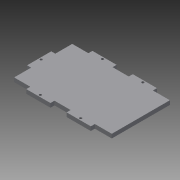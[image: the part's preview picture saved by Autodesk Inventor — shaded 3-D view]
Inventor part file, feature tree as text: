
AUTODESK INVENTOR PART (.ipt)
format: ipt  version: 2014 (Build 180170000, 170)  size: 110,080 bytes
history: native  units: mm
features: reference x4, extrude x1, sketch x1
ambient origin geometry x8: Origin, YZ Plane, XZ Plane, XY Plane, X Axis, Y Axis, Z Axis, Center Point
bodies: 实体1 (feature_tree)
feature tree (6):
  extrude  "拉伸1"  Depth=30.0mm
  sketch  "草图1"  dims[d0=30.0mm d1=30.0mm d2=20.0mm d3=20.0mm d4=5.0mm d5=30.0mm d6=5.0mm d7=3.0mm d8=3.0mm d9=3.0mm d10=3.0mm d11=3.0mm d12=5.0mm d13=0.0mm]
  reference  "参考1"
  reference  "参考2"
  reference  "参考3"
  reference  "参考4"
